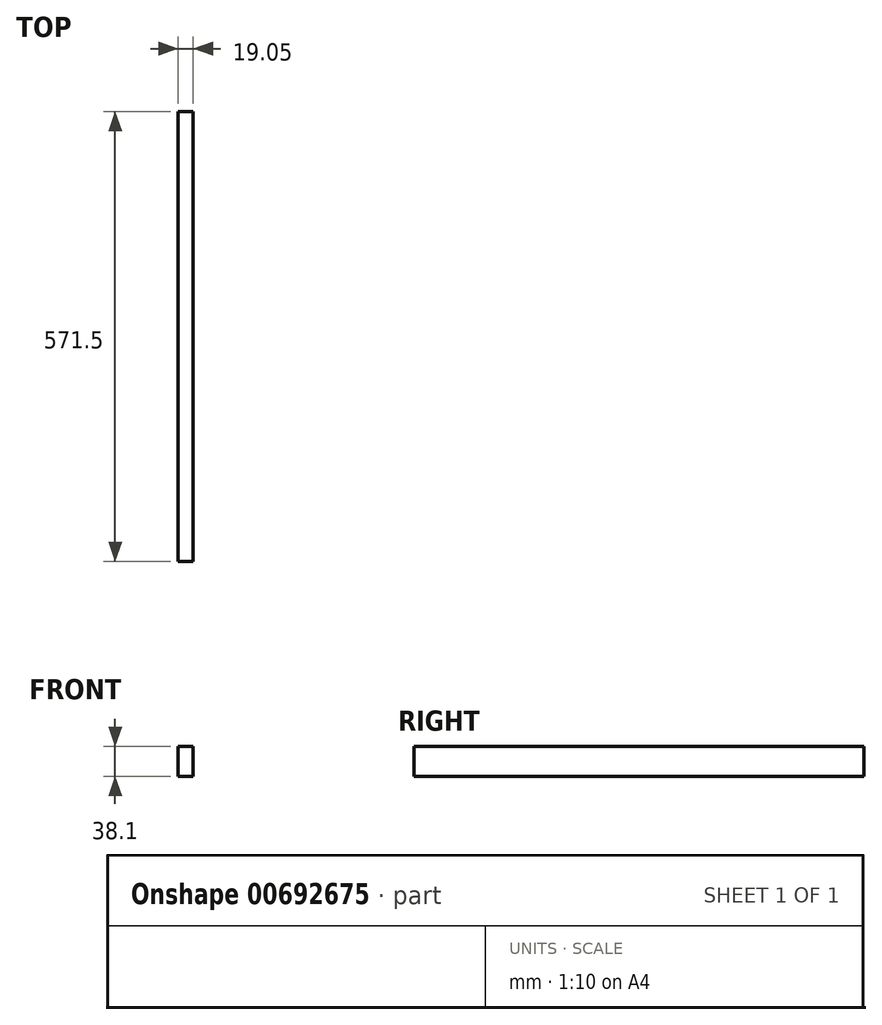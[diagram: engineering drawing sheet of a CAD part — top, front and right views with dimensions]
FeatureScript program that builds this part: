
annotation { "Feature Type Name" : "Feature", "Feature Type Description" : "" }
export const myFeature = defineFeature(function(context is Context, id is Id, definition is map)
    precondition{}
    {
        {
            var Q0;
            Q0=qCreatedBy(makeId("Top.planeOp"),FACE);
            var sketch = newSketch(context, id + "F0", { "sketchPlane" : qUnion([Q0])});
            skLineSegment(sketch, "E0.bottom", {"start": v(0, 0) * mm, "end": v(19.05, 0) * mm});
            skLineSegment(sketch, "E0.top", {"start": v(0, -571.5) * mm, "end": v(19.05, -571.5) * mm});
            skLineSegment(sketch, "E0.left", {"start": v(0, 0) * mm, "end": v(0, -571.5) * mm});
            skLineSegment(sketch, "E0.right", {"start": v(19.05, 0) * mm, "end": v(19.05, -571.5) * mm});
            skSolve(sketch);
        }
        {
            var Q0;
            Q0=makeQuery(id+"F0.imprint","IMPRINT",FACE,{"disambiguationData":[TD([[makeQuery(id+"F0.imprint","IMPRINT",EDGE,{"derivedFrom":sQuery(id+"F0.wireOp",EDGE,"E0.bottom")}),-1.0]])]});
            extrude(context, id + "F1", {"entities" : qUnion([Q0]), "depth" : 38.1 * mm, "offsetDistance" : 25.4 * mm});
        }
    });
